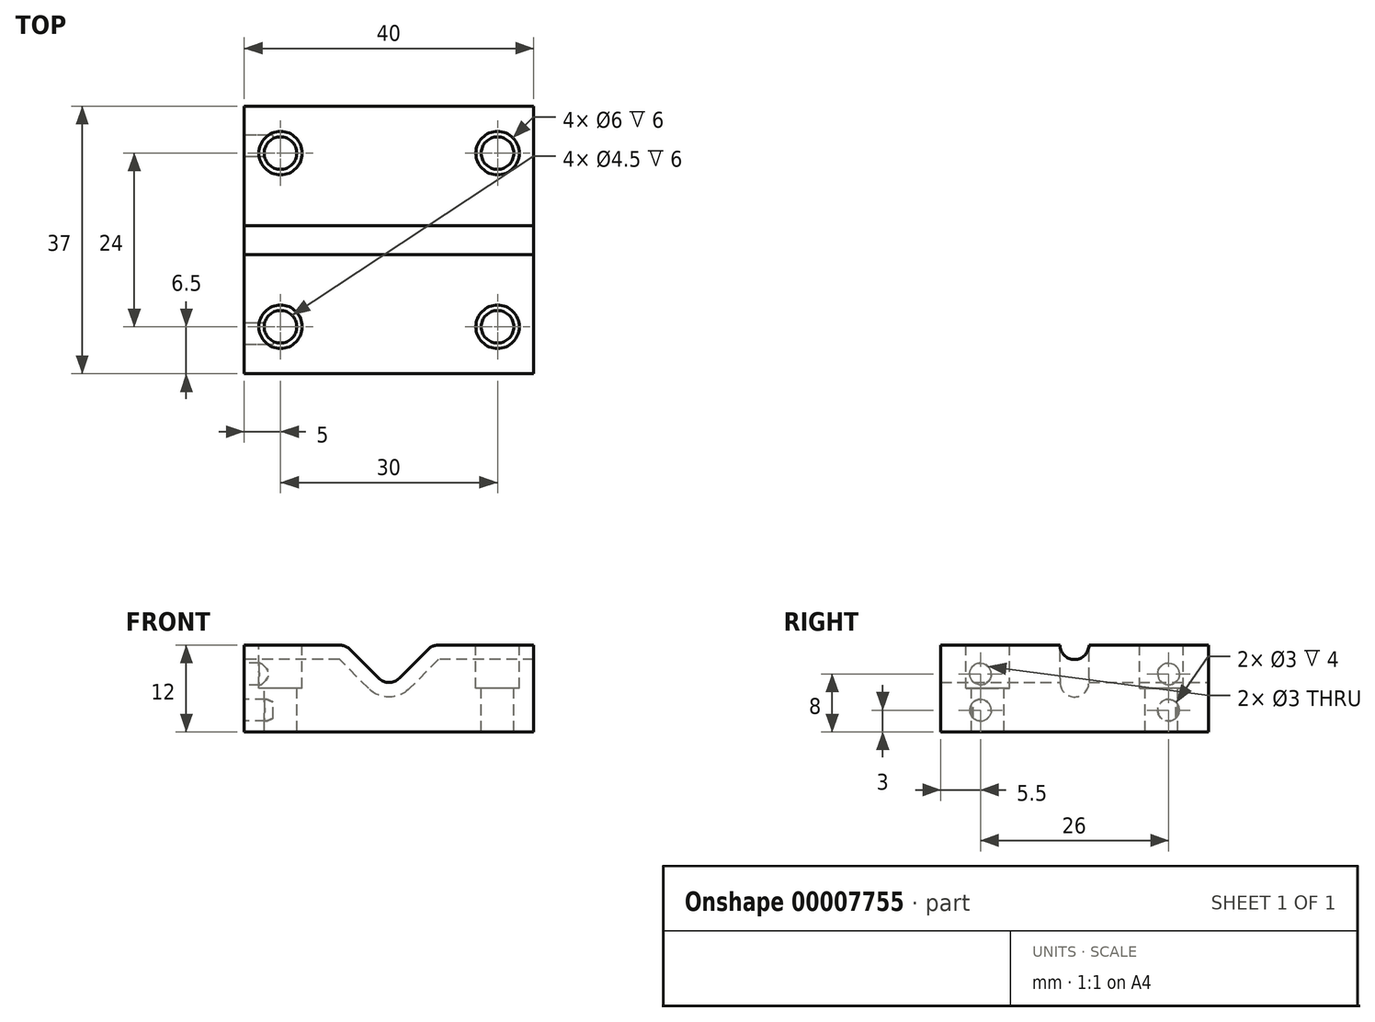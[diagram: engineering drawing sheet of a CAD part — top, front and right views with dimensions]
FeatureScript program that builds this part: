
annotation { "Feature Type Name" : "Feature", "Feature Type Description" : "" }
export const myFeature = defineFeature(function(context is Context, id is Id, definition is map)
    precondition{}
    {
        {
            var Q0;
            Q0=qCreatedBy(makeId("Front.planeOp"),FACE);
            var sketch = newSketch(context, id + "F0", { "sketchPlane" : qUnion([Q0])});
            skLineSegment(sketch, "E0.rect.bottom", {"start": v(-20, -6) * mm, "end": v(20, -6) * mm});
            skLineSegment(sketch, "E0.rect.top", {"start": v(-20, 6) * mm, "end": v(-6.83, 6) * mm});
            skLineSegment(sketch, "E0.rect.left", {"start": v(-20, -6) * mm, "end": v(-20, 6) * mm});
            skLineSegment(sketch, "E0.rect.right", {"start": v(20, -6) * mm, "end": v(20, 6) * mm});
            skPoint(sketch, "E0.rect.middle", {"position": v(0, 0) * mm});
            skLineSegment(sketch, "E1", {"start": v(-1.41, 1.41) * mm, "end": v(-5.41, 5.41) * mm});
            skLineSegment(sketch, "E2", {"start": v(5.41, 5.41) * mm, "end": v(1.41, 1.41) * mm});
            skArc(sketch, "E3.filletArc", {"start": v(-1.41, 1.41) * mm, "mid": v(0, 0.83) * mm, "end": v(1.41, 1.41) * mm});
            skLineSegment(sketch, "E4.trimOffspring", {"start": v(6.83, 6) * mm, "end": v(20, 6) * mm});
            skPoint(sketch, "E5.visualSharp", {"position": v(-6, 6) * mm});
            skArc(sketch, "E5.filletArc", {"start": v(-5.41, 5.41) * mm, "mid": v(-6.06, 5.85) * mm, "end": v(-6.83, 6) * mm});
            skPoint(sketch, "E6.visualSharp", {"position": v(6, 6) * mm});
            skArc(sketch, "E6.filletArc", {"start": v(6.83, 6) * mm, "mid": v(6.06, 5.85) * mm, "end": v(5.41, 5.41) * mm});
            skSolve(sketch);
        }
        {
            var Q0;
            Q0 = qSketchRegion(id + "F0", true);
            extrude(context, id + "F1", {"entities" : qUnion([Q0]), "endBound" : BoundingType.SYMMETRIC, "depth" : 37 * mm});
        }
        {
            var Q0;
            Q0=makeQuery(id+"F1.opExtrude","SWEPT_FACE",FACE,{"disambiguationData":[OSD([sQuery(id+"F0.wireOp",EDGE,"E0.rect.right")])]});
            var sketch = newSketch(context, id + "F2", { "sketchPlane" : qUnion([Q0])});
            skCircle(sketch, "E7", {"center": v(0, 6) * mm, "radius": 2 * mm});
            skSolve(sketch);
        }
        {
            var Q0;
            Q0=qCreatedBy(makeId("Front.planeOp"),FACE);
            var sketch = newSketch(context, id + "F3", { "sketchPlane" : qUnion([Q0])});
            skLineSegment(sketch, "E8.0", {"start": v(6.83, 6) * mm, "end": v(20, 6) * mm});
            skArc(sketch, "E8.1", {"start": v(6.83, 6) * mm, "mid": v(6.06, 5.85) * mm, "end": v(5.41, 5.41) * mm});
            skLineSegment(sketch, "E8.2", {"start": v(5.41, 5.41) * mm, "end": v(1.41, 1.41) * mm});
            skArc(sketch, "E8.3", {"start": v(-1.41, 1.41) * mm, "mid": v(0, 0.83) * mm, "end": v(1.41, 1.41) * mm});
            skLineSegment(sketch, "E8.4", {"start": v(-1.41, 1.41) * mm, "end": v(-5.41, 5.41) * mm});
            skArc(sketch, "E8.5", {"start": v(-5.41, 5.41) * mm, "mid": v(-6.06, 5.85) * mm, "end": v(-6.83, 6) * mm});
            skLineSegment(sketch, "E8.6", {"start": v(-20, 6) * mm, "end": v(-6.83, 6) * mm});
            skSolve(sketch);
        }
        {
            var Q0;
            {var subQ0=makeQuery(id+"F1.opExtrude","SWEPT_EDGE",EDGE,{"disambiguationData":[OSD([sQuery(id+"F0.wireOp",EDGE,"E0.rect.right"),sQuery(id+"F0.wireOp",EDGE,"E4.trimOffspring")])]});var subQ1=sQuery(id+"F2.wireOp",EDGE,"E7");var subQ3=makeQuery(id+"F2.imprint","INTERSECT",VERTEX,{"disambiguationData":[OD(0.0)],"derivedFrom":[subQ0,subQ1]});Q0=makeQuery(id+"F2.imprint","IMPRINT",FACE,{"disambiguationData":[TD([[makeQuery(id+"F2.imprint","IMPRINT",EDGE,{"disambiguationData":[TD([[subQ3,-1.0]])],"derivedFrom":subQ1}),1.0]])]});}
            var Q1;
            {var subQ0=makeQuery(id+"F1.opExtrude","SWEPT_EDGE",EDGE,{"disambiguationData":[OSD([sQuery(id+"F0.wireOp",EDGE,"E0.rect.right"),sQuery(id+"F0.wireOp",EDGE,"E4.trimOffspring")])]});var subQ1=sQuery(id+"F2.wireOp",EDGE,"E7");var subQ3=makeQuery(id+"F2.imprint","INTERSECT",VERTEX,{"disambiguationData":[OD(0.0)],"derivedFrom":[subQ0,subQ1]});Q1=makeQuery(id+"F2.imprint","IMPRINT",FACE,{"disambiguationData":[TD([[makeQuery(id+"F2.imprint","IMPRINT",EDGE,{"disambiguationData":[TD([[subQ3,1.0]])],"derivedFrom":subQ1}),1.0]])]});}
            var Q2;
            Q2=sQuery(id+"F3.wireOp",EDGE,"E8.0");
            var Q3;
            Q3=sQuery(id+"F3.wireOp",EDGE,"E8.1");
            var Q4;
            Q4=sQuery(id+"F3.wireOp",EDGE,"E8.2");
            var Q5;
            Q5=sQuery(id+"F3.wireOp",EDGE,"E8.3");
            var Q6;
            Q6=sQuery(id+"F3.wireOp",EDGE,"E8.4");
            var Q7;
            Q7=sQuery(id+"F3.wireOp",EDGE,"E8.5");
            var Q8;
            Q8=sQuery(id+"F3.wireOp",EDGE,"E8.6");
            sweep(context, id + "F4", {"operationType" : NewBodyOperationType.REMOVE, "profiles" : qUnion([Q0, Q1]), "path" : qUnion([Q2, Q3, Q4, Q5, Q6, Q7, Q8])});
        }
        {
            var Q0;
            {var subQ0=sQuery(id+"F0.wireOp",EDGE,"E0.rect.top");var subQ2=sQuery(id+"F0.wireOp",EDGE,"E5.filletArc");var subQ3=sQuery(id+"F0.wireOp",EDGE,"E0.rect.left");Q0=makeQuery(id+"F4.boolean.opBoolean","SPLIT",FACE,{"disambiguationData":[TD([makeQuery(id+"F1.opExtrude","CAP_FACE",FACE,{"disambiguationData":[OSD([sQuery(id+"F0.wireOp",EDGE,"E0.rect.bottom"),subQ0,subQ3,sQuery(id+"F0.wireOp",EDGE,"E0.rect.right"),sQuery(id+"F0.wireOp",EDGE,"E1"),sQuery(id+"F0.wireOp",EDGE,"E2"),sQuery(id+"F0.wireOp",EDGE,"E3.filletArc"),sQuery(id+"F0.wireOp",EDGE,"E4.trimOffspring"),subQ2,sQuery(id+"F0.wireOp",EDGE,"E6.filletArc")])],"isStart":false})])],"derivedFrom":makeQuery(id+"F1.opExtrude","SWEPT_FACE",FACE,{"disambiguationData":[OSD([subQ0])]})});}
            var sketch = newSketch(context, id + "F5", { "sketchPlane" : qUnion([Q0])});
            skCircle(sketch, "E9", {"center": v(-15, 12) * mm, "radius": 3 * mm});
            skCircle(sketch, "E10.0.1.0", {"center": v(-15, -12) * mm, "radius": 3 * mm});
            skCircle(sketch, "E10.1.0.0", {"center": v(15, 12) * mm, "radius": 3 * mm});
            skCircle(sketch, "E10.1.1.0", {"center": v(15, -12) * mm, "radius": 3 * mm});
            skLineSegment(sketch, "E10.direction1", {"start": v(-15, 12) * mm, "end": v(15, 12) * mm, "construction": true});
            skLineSegment(sketch, "E10.direction2", {"start": v(-15, 12) * mm, "end": v(-15, -12) * mm, "construction": true});
            skSolve(sketch);
        }
        {
            var Q0;
            Q0 = qSketchRegion(id + "F5", true);
            extrude(context, id + "F6", {"entities" : qUnion([Q0]), "operationType" : NewBodyOperationType.REMOVE, "oppositeDirection" : true, "depth" : 6 * mm});
        }
        {
            var Q0;
            Q0=makeQuery(id+"F6.boolean.opBoolean","COPY",FACE,{"derivedFrom":makeQuery(id+"F6.opExtrude","CAP_FACE",FACE,{"disambiguationData":[OSD([sQuery(id+"F5.wireOp",EDGE,"E10.0.1.0")])],"isStart":false})});
            var sketch = newSketch(context, id + "F7", { "sketchPlane" : qUnion([Q0])});
            skCircle(sketch, "E11", {"center": v(-15, -12) * mm, "radius": 2.25 * mm});
            skCircle(sketch, "E12.0.1.0", {"center": v(-15, 12) * mm, "radius": 2.25 * mm});
            skCircle(sketch, "E12.1.0.0", {"center": v(15, -12) * mm, "radius": 2.25 * mm});
            skCircle(sketch, "E12.1.1.0", {"center": v(15, 12) * mm, "radius": 2.25 * mm});
            skLineSegment(sketch, "E12.direction1", {"start": v(-15, -12) * mm, "end": v(15, -12) * mm, "construction": true});
            skLineSegment(sketch, "E12.direction2", {"start": v(-15, -12) * mm, "end": v(-15, 12) * mm, "construction": true});
            skSolve(sketch);
        }
        {
            var Q0;
            Q0 = qSketchRegion(id + "F7", true);
            extrude(context, id + "F8", {"entities" : qUnion([Q0]), "operationType" : NewBodyOperationType.REMOVE, "endBound" : BoundingType.THROUGH_ALL, "oppositeDirection" : true, "depth" : 25 * mm});
        }
        {
            var Q0;
            Q0=makeQuery(id+"F1.opExtrude","SWEPT_FACE",FACE,{"disambiguationData":[OSD([sQuery(id+"F0.wireOp",EDGE,"E0.rect.left")])]});
            var sketch = newSketch(context, id + "F9", { "sketchPlane" : qUnion([Q0])});
            skCircle(sketch, "E13", {"center": v(-13, -3) * mm, "radius": 1.5 * mm});
            skCircle(sketch, "E14", {"center": v(-13, 2) * mm, "radius": 1.5 * mm});
            skCircle(sketch, "E15", {"center": v(13, -3) * mm, "radius": 1.5 * mm});
            skCircle(sketch, "E16", {"center": v(13, 2) * mm, "radius": 1.5 * mm});
            skSolve(sketch);
        }
        {
            var Q0;
            Q0 = qSketchRegion(id + "F9", true);
            extrude(context, id + "F10", {"entities" : qUnion([Q0]), "operationType" : NewBodyOperationType.REMOVE, "oppositeDirection" : true, "depth" : 4 * mm});
        }
    });
